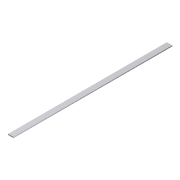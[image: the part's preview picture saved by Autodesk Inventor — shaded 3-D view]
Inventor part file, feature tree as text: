
AUTODESK INVENTOR PART (.ipt)
format: ipt  version: 2012 (Build 160160000, 160)  size: 61,440 bytes
history: native  units: in
note: dims shown in document units (in); Inventor stores cm internally (conversion verified against a paired STEP export)
features: extrude x1, sketch x1
ambient origin geometry x8: Origin, YZ Plane, XZ Plane, XY Plane, X Axis, Y Axis, Z Axis, Center Point
bodies: Solid1 (feature_tree)
feature tree (2):
  extrude  "Extrusion1"  Depth=0.5in
  sketch  "Sketch1"  dims[d0=0.0938in d1=0.5in d2=14.75in d3=0.0in]
